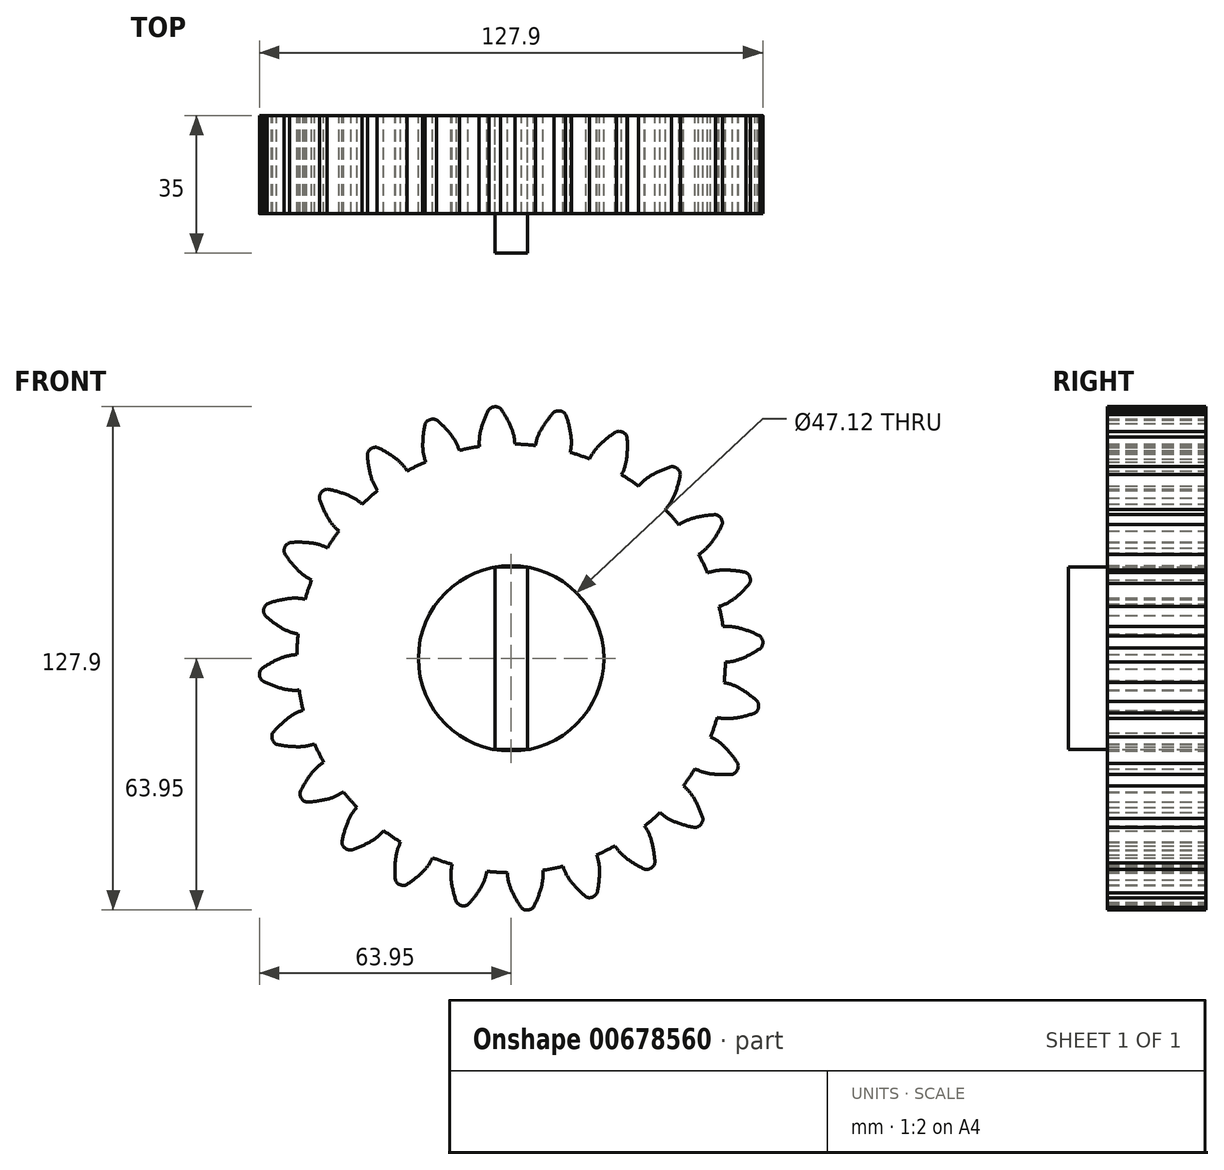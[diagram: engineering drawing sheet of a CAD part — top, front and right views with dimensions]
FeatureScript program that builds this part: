
annotation { "Feature Type Name" : "Feature", "Feature Type Description" : "" }
export const myFeature = defineFeature(function(context is Context, id is Id, definition is map)
    precondition{}
    {
        {
            var Q0;
            Q0=qCreatedBy(makeId("Front.planeOp"),FACE);
            var sketch = newSketch(context, id + "F0", { "sketchPlane" : qUnion([Q0])});
            skCircle(sketch, "E0", {"center": v(0, 0) * mm, "radius": 54.45 * mm});
            skCircle(sketch, "E1", {"center": v(0, 0) * mm, "radius": 58.67 * mm, "construction": true});
            skCircle(sketch, "E2", {"center": v(0, 0) * mm, "radius": 63.5 * mm, "construction": true});
            skLineSegment(sketch, "E3", {"start": v(0, 0) * mm, "end": v(0, 62.72) * mm, "construction": true});
            skLineSegment(sketch, "E4", {"start": v(0, 0) * mm, "end": v(-0.67, 62.72) * mm, "construction": true});
            skLineSegment(sketch, "E5", {"start": v(0, 58.67) * mm, "end": v(-81.07, 58.67) * mm, "construction": true});
            skLineSegment(sketch, "E6", {"start": v(0, 58.67) * mm, "end": v(-75.05, 31.36) * mm, "construction": true});
            skPoint(sketch, "E6.endSnap0", {"position": v(-0.34, 31.36) * mm});
            skCircle(sketch, "E7", {"center": v(0, 0) * mm, "radius": 55.14 * mm, "construction": true});
            skCircle(sketch, "E8", {"center": v(0, 58.67) * mm, "radius": 18.57 * mm, "construction": true});
            skLineSegment(sketch, "E9", {"start": v(0, 0) * mm, "end": v(-5.28, 80.55) * mm, "construction": true});
            skCircle(sketch, "E10", {"center": v(-17.44, 52.3) * mm, "radius": 18.53 * mm, "construction": true});
            skArc(sketch, "E11", {"start": v(0, 58.67) * mm, "mid": v(-1.2, 61.13) * mm, "end": v(-2.64, 63.44) * mm});
            skArc(sketch, "E12", {"start": v(0.96, 54.44) * mm, "mid": v(0.67, 56.6) * mm, "end": v(0, 58.67) * mm});
            skArc(sketch, "E13.MirrorCS", {"start": v(-7.66, 58.17) * mm, "mid": v(-6.8, 60.76) * mm, "end": v(-5.66, 63.25) * mm});
            skArc(sketch, "E14.MirrorCS", {"start": v(-8.05, 53.85) * mm, "mid": v(-8.05, 56.03) * mm, "end": v(-7.66, 58.17) * mm});
            skArc(sketch, "E15", {"start": v(-2.64, 63.44) * mm, "mid": v(-4.2, 63.94) * mm, "end": v(-5.66, 63.25) * mm});
            skCircle(sketch, "E16", {"center": v(0, 0) * mm, "radius": 23.56 * mm});
            skLineSegment(sketch, "E17.bottom", {"start": v(-4.14, 23.2) * mm, "end": v(4.14, 23.2) * mm});
            skLineSegment(sketch, "E17.top", {"start": v(-4.14, -23.2) * mm, "end": v(4.14, -23.2) * mm});
            skLineSegment(sketch, "E17.left", {"start": v(-4.14, 23.2) * mm, "end": v(-4.14, -23.2) * mm});
            skLineSegment(sketch, "E17.right", {"start": v(4.14, 23.2) * mm, "end": v(4.14, -23.2) * mm});
            skSolve(sketch);
        }
        {
            var Q0;
            {var subQ0=sQuery(id+"F0.wireOp",EDGE,"E0");var subQ1=makeQuery(id+"F0.imprint","INTERSECT",VERTEX,{"derivedFrom":[subQ0,sQuery(id+"F0.wireOp",EDGE,"E12")]});Q0=makeQuery(id+"F0.imprint","IMPRINT",FACE,{"disambiguationData":[TD([[makeQuery(id+"F0.imprint","IMPRINT",EDGE,{"disambiguationData":[TD([[subQ1,-1.0]])],"derivedFrom":subQ0}),1.0]])]});}
            var Q1;
            Q1=makeQuery(id+"F0.imprint","IMPRINT",FACE,{"disambiguationData":[TD([[makeQuery(id+"F0.imprint","IMPRINT",EDGE,{"derivedFrom":sQuery(id+"F0.wireOp",EDGE,"E11")}),1.0]])]});
            extrude(context, id + "F1", {"entities" : qUnion([Q0, Q1]), "depth" : 25 * mm, "offsetDistance" : 25 * mm});
        }
        {
            var Q0;
            Q0=makeQuery(id+"F1.opExtrude","SWEPT_BODY",BODY,{"disambiguationData":[OSD([sQuery(id+"F0.wireOp",EDGE,"E0"),sQuery(id+"F0.wireOp",EDGE,"E11"),sQuery(id+"F0.wireOp",EDGE,"E12"),sQuery(id+"F0.wireOp",EDGE,"E13.MirrorCS"),sQuery(id+"F0.wireOp",EDGE,"E14.MirrorCS"),sQuery(id+"F0.wireOp",EDGE,"E15")])]});
            var Q1;
            Q1=makeQuery(id+"F1.opExtrude","SWEPT_FACE",FACE,{"disambiguationData":[OSD([sQuery(id+"F0.wireOp",EDGE,"E0")])]});
            circularPattern(context, id + "F2", {"entities" : qUnion([Q0]), "axis" : qUnion([Q1]), "angle" : 360 * degree, "instanceCount" : 24, "equalSpace" : true});
        }
        {
            var Q0;
            Q0=makeQuery(id+"F0.imprint","IMPRINT",FACE,{"disambiguationData":[TD([[makeQuery(id+"F0.imprint","IMPRINT",EDGE,{"derivedFrom":sQuery(id+"F0.wireOp",EDGE,"E17.bottom")}),-1.0]])]});
            extrude(context, id + "F3", {"entities" : qUnion([Q0]), "operationType" : NewBodyOperationType.ADD, "depth" : 35 * mm, "offsetDistance" : 25 * mm});
        }
    });
